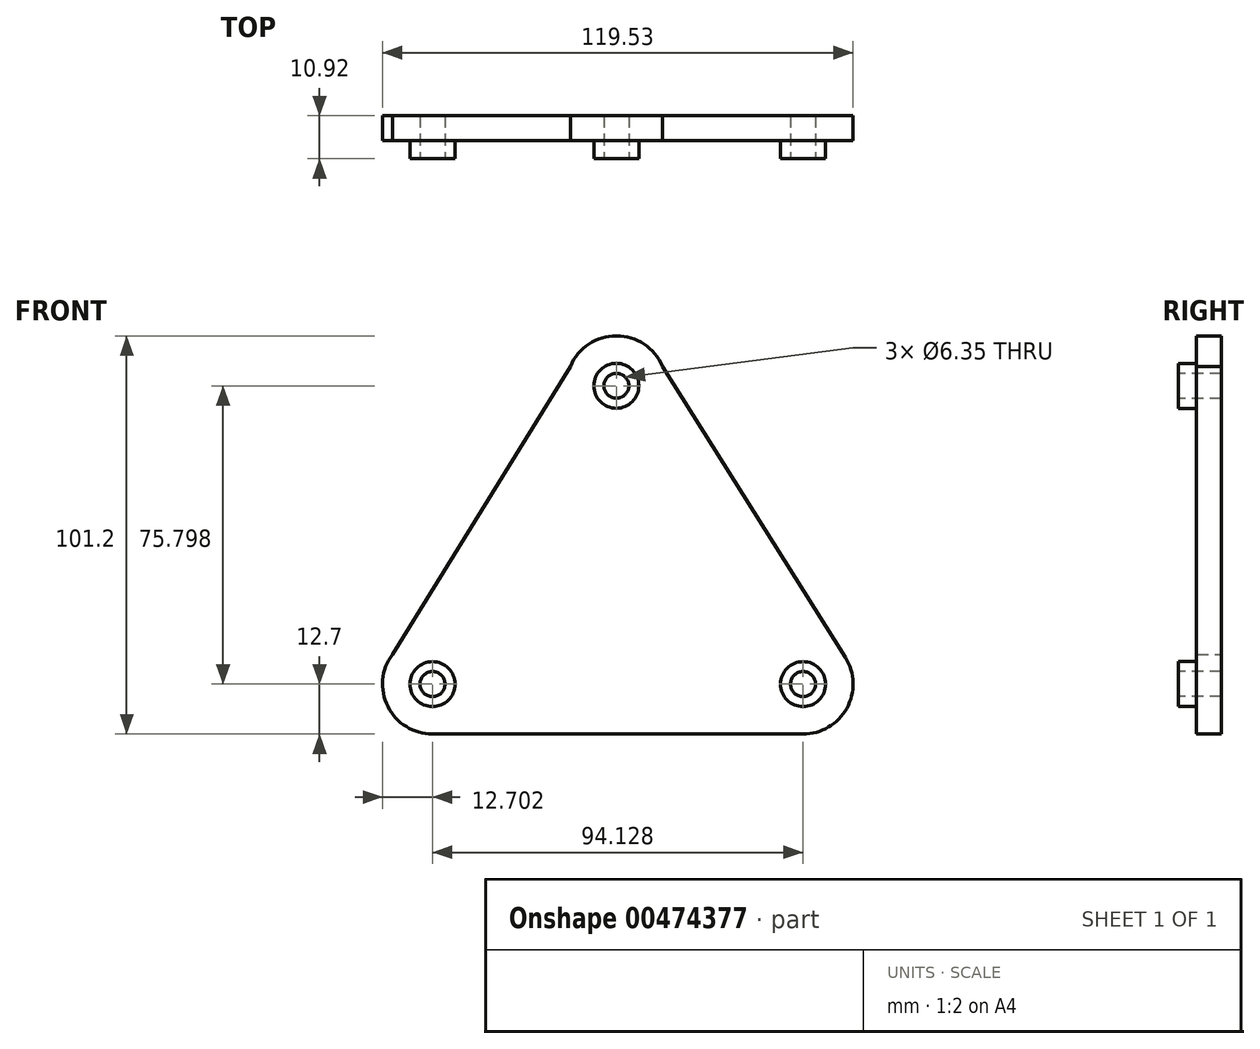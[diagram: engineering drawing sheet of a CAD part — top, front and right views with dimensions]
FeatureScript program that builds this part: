
annotation { "Feature Type Name" : "Feature", "Feature Type Description" : "" }
export const myFeature = defineFeature(function(context is Context, id is Id, definition is map)
    precondition{}
    {
        {
            var Q0;
            Q0=qCreatedBy(makeId("Front.planeOp"),FACE);
            var sketch = newSketch(context, id + "F0", { "sketchPlane" : qUnion([Q0])});
            skCircle(sketch, "E0", {"center": v(0, 75.8) * mm, "radius": 12.7 * mm});
            skCircle(sketch, "E1", {"center": v(47.42, 0) * mm, "radius": 12.7 * mm});
            skCircle(sketch, "E2", {"center": v(-46.7, 0) * mm, "radius": 12.7 * mm});
            skLineSegment(sketch, "E3", {"start": v(11.7, 80.75) * mm, "end": v(58.17, 6.76) * mm});
            skLineSegment(sketch, "E4", {"start": v(58.17, 6.76) * mm, "end": v(47.42, -12.7) * mm});
            skLineSegment(sketch, "E5", {"start": v(47.42, -12.7) * mm, "end": v(-46.7, -12.7) * mm});
            skLineSegment(sketch, "E6", {"start": v(-46.7, -12.7) * mm, "end": v(-56.91, 7.56) * mm});
            skLineSegment(sketch, "E7", {"start": v(-56.91, 7.56) * mm, "end": v(-11.7, 80.75) * mm});
            skSolve(sketch);
        }
        {
            var Q0;
            Q0 = qSketchRegion(id + "F0", true);
            extrude(context, id + "F1", {"entities" : qUnion([Q0]), "depth" : 6.35 * mm});
        }
        {
            var Q0;
            Q0=makeQuery(id+"F1.opExtrude","CAP_FACE",FACE,{"disambiguationData":[OSD([sQuery(id+"F0.wireOp",EDGE,"E0"),sQuery(id+"F0.wireOp",EDGE,"E1"),sQuery(id+"F0.wireOp",EDGE,"E2"),sQuery(id+"F0.wireOp",EDGE,"E3"),sQuery(id+"F0.wireOp",EDGE,"E5"),sQuery(id+"F0.wireOp",EDGE,"E7")])],"isStart":false});
            var sketch = newSketch(context, id + "F2", { "sketchPlane" : qUnion([Q0])});
            skCircle(sketch, "E8", {"center": v(0, 75.8) * mm, "radius": 3.18 * mm});
            skCircle(sketch, "E9", {"center": v(47.42, 0) * mm, "radius": 3.18 * mm});
            skCircle(sketch, "E10", {"center": v(-46.7, 0) * mm, "radius": 3.18 * mm});
            skCircle(sketch, "E11.0", {"center": v(0, 75.8) * mm, "radius": 5.72 * mm});
            skCircle(sketch, "E12.0", {"center": v(47.42, 0) * mm, "radius": 5.72 * mm});
            skCircle(sketch, "E13.0", {"center": v(-46.7, 0) * mm, "radius": 5.72 * mm});
            skSolve(sketch);
        }
        {
            var Q0;
            Q0=makeQuery(id+"F2.imprint","IMPRINT",FACE,{"disambiguationData":[TD([[makeQuery(id+"F2.imprint","IMPRINT",EDGE,{"derivedFrom":sQuery(id+"F2.wireOp",EDGE,"E10")}),1.0]])]});
            var Q1;
            Q1=makeQuery(id+"F2.imprint","IMPRINT",FACE,{"disambiguationData":[TD([[makeQuery(id+"F2.imprint","IMPRINT",EDGE,{"derivedFrom":sQuery(id+"F2.wireOp",EDGE,"E9")}),1.0]])]});
            var Q2;
            Q2=makeQuery(id+"F2.imprint","IMPRINT",FACE,{"disambiguationData":[TD([[makeQuery(id+"F2.imprint","IMPRINT",EDGE,{"derivedFrom":sQuery(id+"F2.wireOp",EDGE,"E8")}),1.0]])]});
            extrude(context, id + "F3", {"entities" : qUnion([Q0, Q1, Q2]), "operationType" : NewBodyOperationType.REMOVE, "oppositeDirection" : true, "depth" : 25.4 * mm});
        }
        {
            var Q0;
            Q0=makeQuery(id+"F2.imprint","IMPRINT",FACE,{"disambiguationData":[TD([[makeQuery(id+"F2.imprint","IMPRINT",EDGE,{"derivedFrom":sQuery(id+"F2.wireOp",EDGE,"E9")}),-1.0]])]});
            var Q1;
            Q1=makeQuery(id+"F2.imprint","IMPRINT",FACE,{"disambiguationData":[TD([[makeQuery(id+"F2.imprint","IMPRINT",EDGE,{"derivedFrom":sQuery(id+"F2.wireOp",EDGE,"E10")}),-1.0]])]});
            var Q2;
            Q2=makeQuery(id+"F2.imprint","IMPRINT",FACE,{"disambiguationData":[TD([[makeQuery(id+"F2.imprint","IMPRINT",EDGE,{"derivedFrom":sQuery(id+"F2.wireOp",EDGE,"E8")}),-1.0]])]});
            extrude(context, id + "F4", {"entities" : qUnion([Q0, Q1, Q2]), "operationType" : NewBodyOperationType.ADD, "depth" : 4.57 * mm});
        }
    });
